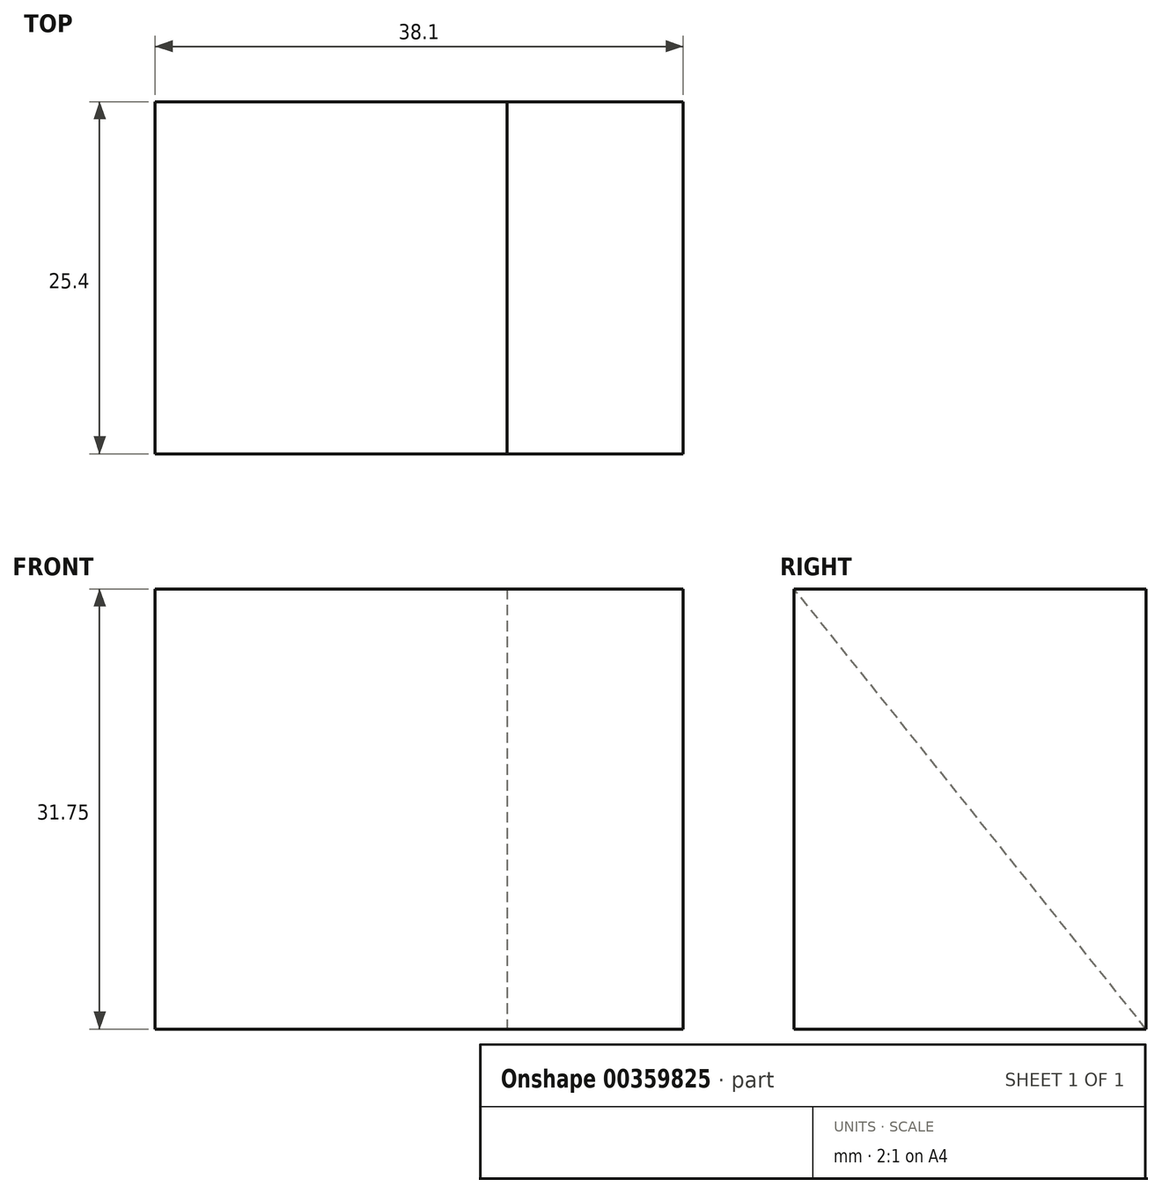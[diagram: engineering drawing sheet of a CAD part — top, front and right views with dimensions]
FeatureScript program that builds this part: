
annotation { "Feature Type Name" : "Feature", "Feature Type Description" : "" }
export const myFeature = defineFeature(function(context is Context, id is Id, definition is map)
    precondition{}
    {
        {
            var Q0;
            Q0=qCreatedBy(makeId("Front.planeOp"),FACE);
            var sketch = newSketch(context, id + "F0", { "sketchPlane" : qUnion([Q0])});
            skLineSegment(sketch, "E0", {"start": v(0, 0) * mm, "end": v(38.1, 0) * mm});
            skLineSegment(sketch, "E1", {"start": v(38.1, 0) * mm, "end": v(38.1, 31.75) * mm});
            skLineSegment(sketch, "E2", {"start": v(38.1, 31.75) * mm, "end": v(0, 31.75) * mm});
            skLineSegment(sketch, "E3", {"start": v(0, 31.75) * mm, "end": v(0, 0) * mm});
            skSolve(sketch);
        }
        {
            var Q0;
            Q0 = qSketchRegion(id + "F0", true);
            var Q1;
            Q1=makeQuery(id+"F0.imprint","IMPRINT",FACE,{"disambiguationData":[TD([[makeQuery(id+"F0.imprint","IMPRINT",EDGE,{"derivedFrom":sQuery(id+"F0.wireOp",EDGE,"E0")}),1.0]])]});
            extrude(context, id + "F1", {"entities" : qUnion([Q0, Q1]), "depth" : 25.4 * mm});
        }
        {
            var Q0;
            Q0=makeQuery(id+"F1.opExtrude","SWEPT_FACE",FACE,{"disambiguationData":[OSD([sQuery(id+"F0.wireOp",EDGE,"E3")])]});
            var sketch = newSketch(context, id + "F2", { "sketchPlane" : qUnion([Q0])});
            skLineSegment(sketch, "E4", {"start": v(0, 0) * mm, "end": v(25.4, 31.75) * mm});
            skSolve(sketch);
        }
        {
            var Q0;
            Q0 = qSketchRegion(id + "F2", true);
            var Q1;
            Q1=makeQuery(id+"F2.imprint","IMPRINT",FACE,{"disambiguationData":[TD([[makeQuery(id+"F2.imprint","IMPRINT",EDGE,{"derivedFrom":sQuery(id+"F2.wireOp",EDGE,"E4")}),1.0]])]});
            extrude(context, id + "F3", {"entities" : qUnion([Q0, Q1]), "operationType" : NewBodyOperationType.REMOVE, "oppositeDirection" : true, "depth" : 25.4 * mm});
        }
    });
